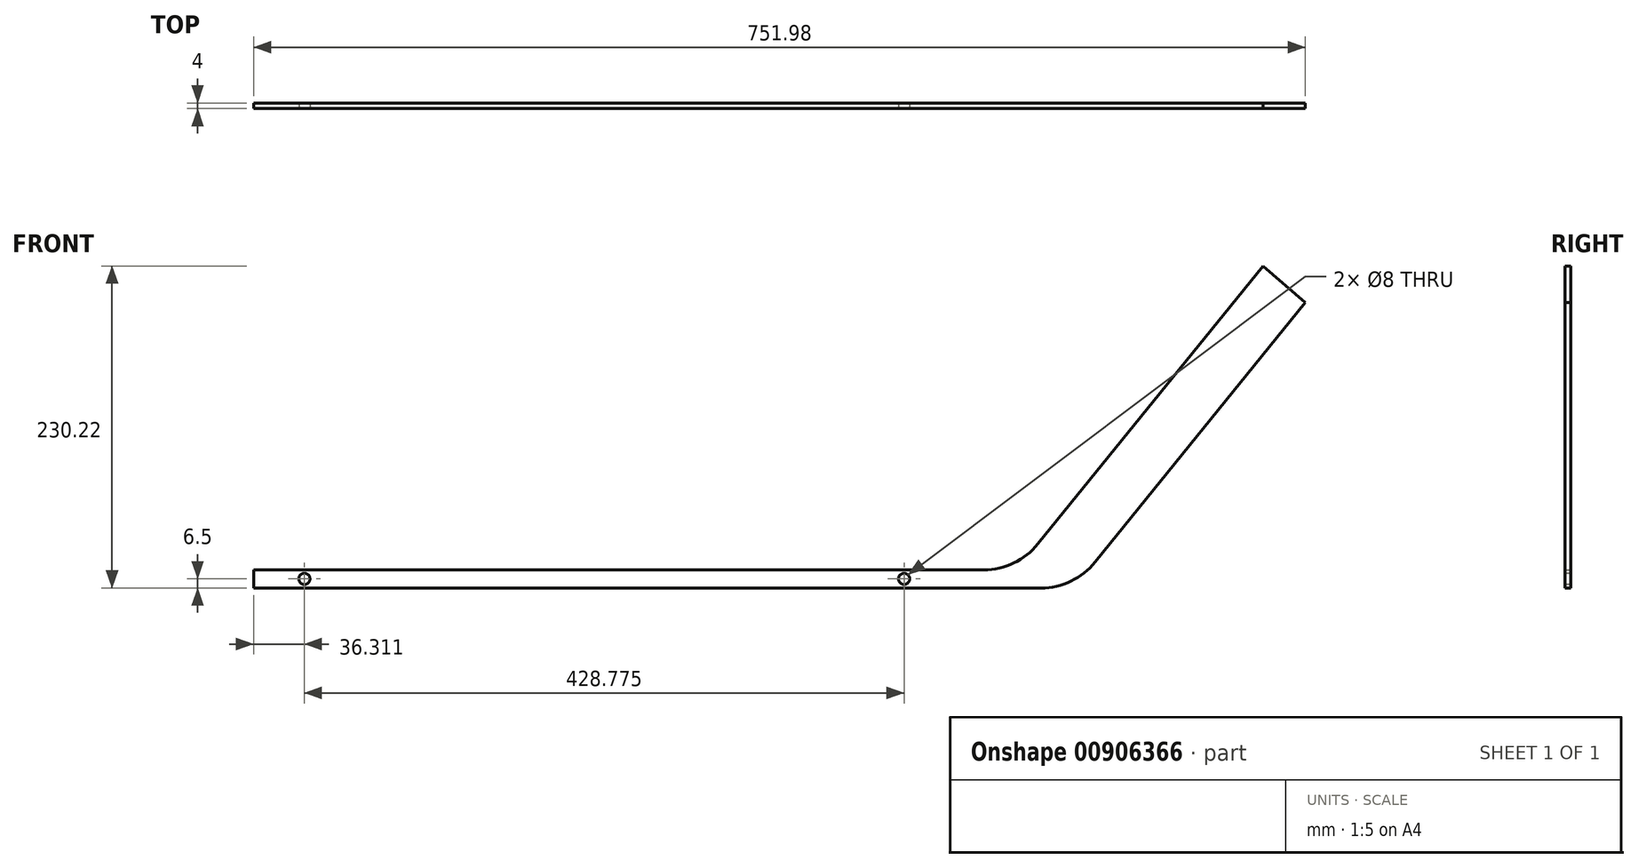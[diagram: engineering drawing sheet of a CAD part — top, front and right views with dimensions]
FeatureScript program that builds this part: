
annotation { "Feature Type Name" : "Feature", "Feature Type Description" : "" }
export const myFeature = defineFeature(function(context is Context, id is Id, definition is map)
    precondition{}
    {
        {
            var Q0;
            Q0=qCreatedBy(makeId("Front.planeOp"),FACE);
            var sketch = newSketch(context, id + "F0", { "sketchPlane" : qUnion([Q0])});
            skLineSegment(sketch, "E0", {"start": v(-219.3, 0) * mm, "end": v(343.67, 0) * mm});
            skLineSegment(sketch, "E1", {"start": v(382.53, 18.53) * mm, "end": v(532.68, 203.95) * mm});
            skPoint(sketch, "E2.visualSharp", {"position": v(367.52, 0) * mm});
            skArc(sketch, "E2.filletArc", {"start": v(343.67, 0) * mm, "mid": v(365.2, 4.87) * mm, "end": v(382.53, 18.53) * mm});
            skLineSegment(sketch, "E3.2", {"start": v(-219.3, 13) * mm, "end": v(302.73, 13) * mm});
            skLineSegment(sketch, "E4", {"start": v(-219.3, 13) * mm, "end": v(-219.3, 0) * mm});
            skLineSegment(sketch, "E5.0", {"start": v(341.58, 31.53) * mm, "end": v(502.48, 230.22) * mm});
            skArc(sketch, "E6.filletArc", {"start": v(302.73, 13) * mm, "mid": v(324.25, 17.87) * mm, "end": v(341.58, 31.53) * mm});
            skLineSegment(sketch, "E7", {"start": v(502.48, 230.22) * mm, "end": v(532.68, 203.95) * mm});
            skPoint(sketch, "E3.0.end.orphan", {"position": v(523.46, 213.23) * mm});
            skPoint(sketch, "E3.1.end.orphan", {"position": v(372.42, 26.72) * mm});
            skSolve(sketch);
        }
        {
            var Q0;
            Q0=makeQuery(id+"F0.imprint","IMPRINT",FACE,{"disambiguationData":[TD([[makeQuery(id+"F0.imprint","IMPRINT",EDGE,{"derivedFrom":sQuery(id+"F0.wireOp",EDGE,"E0")}),1.0]])]});
            extrude(context, id + "F1", {"entities" : qUnion([Q0]), "depth" : 4 * mm, "offsetDistance" : 25 * mm});
        }
        {
            var Q0;
            Q0=makeQuery(id+"F1.opExtrude","CAP_FACE",FACE,{"disambiguationData":[OSD([sQuery(id+"F0.wireOp",EDGE,"E0"),sQuery(id+"F0.wireOp",EDGE,"E1"),sQuery(id+"F0.wireOp",EDGE,"E2.filletArc"),sQuery(id+"F0.wireOp",EDGE,"E3.0"),sQuery(id+"F0.wireOp",EDGE,"E3.1"),sQuery(id+"F0.wireOp",EDGE,"E3.2"),sQuery(id+"F0.wireOp",EDGE,"5G5G6kUv-I3YN-A78y-infV-ad7Mtm1H1URn"),sQuery(id+"F0.wireOp",EDGE,"E4")])],"isStart":false});
            var sketch = newSketch(context, id + "F2", { "sketchPlane" : qUnion([Q0])});
            skCircle(sketch, "E8", {"center": v(-182.99, 6.5) * mm, "radius": 4 * mm});
            skCircle(sketch, "E9", {"center": v(245.79, 6.5) * mm, "radius": 4 * mm});
            skSolve(sketch);
        }
        {
            var Q0;
            Q0=makeQuery(id+"F2.imprint","IMPRINT",FACE,{"disambiguationData":[TD([[makeQuery(id+"F2.imprint","IMPRINT",EDGE,{"derivedFrom":sQuery(id+"F2.wireOp",EDGE,"E9")}),1.0]])]});
            var Q1;
            Q1=makeQuery(id+"F2.imprint","IMPRINT",FACE,{"disambiguationData":[TD([[makeQuery(id+"F2.imprint","IMPRINT",EDGE,{"derivedFrom":sQuery(id+"F2.wireOp",EDGE,"E8")}),1.0]])]});
            extrude(context, id + "F3", {"entities" : qUnion([Q0, Q1]), "operationType" : NewBodyOperationType.REMOVE, "oppositeDirection" : true, "depth" : 25 * mm, "offsetDistance" : 25 * mm});
        }
    });
